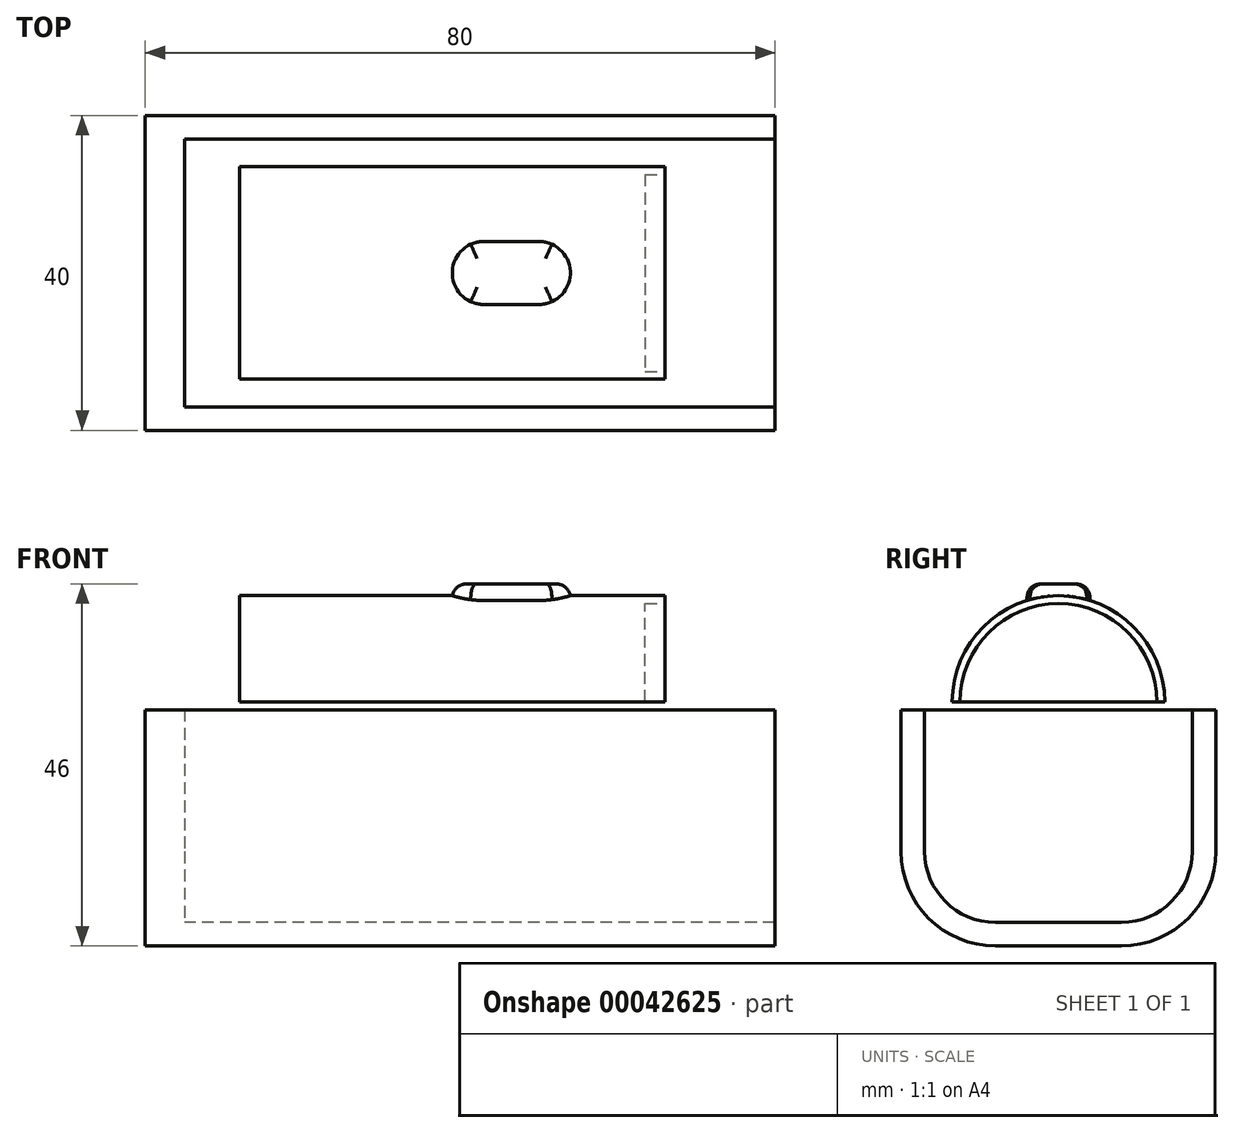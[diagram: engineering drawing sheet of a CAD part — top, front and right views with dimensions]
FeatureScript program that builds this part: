
annotation { "Feature Type Name" : "Feature", "Feature Type Description" : "" }
export const myFeature = defineFeature(function(context is Context, id is Id, definition is map)
    precondition{}
    {
        {
            var Q0;
            Q0=qCreatedBy(makeId("Top.planeOp"),FACE);
            var sketch = newSketch(context, id + "F0", { "sketchPlane" : qUnion([Q0])});
            skCircle(sketch, "E0", {"center": v(0, 0) * mm, "radius": 7 * mm});
            skSolve(sketch);
        }
        {
            var Q0;
            Q0 = qSketchRegion(id + "F0", true);
            extrude(context, id + "F1", {"entities" : qUnion([Q0]), "depth" : 1.5 * mm});
        }
        {
            var Q0;
            Q0=makeQuery(id+"F1.opExtrude","CAP_FACE",FACE,{"disambiguationData":[OSD([sQuery(id+"F0.wireOp",EDGE,"E0")])],"isStart":false});
            var sketch = newSketch(context, id + "F2", { "sketchPlane" : qUnion([Q0])});
            skCircle(sketch, "E1", {"center": v(0, 0) * mm, "radius": 10 * mm});
            skSolve(sketch);
        }
        {
            var Q0;
            Q0 = qSketchRegion(id + "F2", true);
            extrude(context, id + "F3", {"entities" : qUnion([Q0]), "operationType" : NewBodyOperationType.ADD, "depth" : 14 * mm});
        }
        {
            var Q0;
            Q0=qCreatedBy(makeId("Right.planeOp"),FACE);
            var sketch = newSketch(context, id + "F4", { "sketchPlane" : qUnion([Q0])});
            skCircle(sketch, "E2", {"center": v(0, 22) * mm, "radius": 13.5 * mm});
            skSolve(sketch);
        }
        {
            var Q0;
            Q0=makeQuery(id+"F4.imprint","IMPRINT",FACE,{"disambiguationData":[TD([[makeQuery(id+"F4.imprint","IMPRINT",EDGE,{"derivedFrom":sQuery(id+"F4.wireOp",EDGE,"E2")}),1.0]])]});
            extrude(context, id + "F5", {"entities" : qUnion([Q0]), "operationType" : NewBodyOperationType.ADD, "depth" : 36 * mm, "hasSecondDirection" : true, "secondDirectionOppositeDirection" : true, "secondDirectionDepth" : 18 * mm});
        }
        {
            var Q0;
            Q0=makeQuery(id+"F5.opExtrude","CAP_FACE",FACE,{"disambiguationData":[OSD([sQuery(id+"F4.wireOp",EDGE,"E2")])],"isStart":false});
            var sketch = newSketch(context, id + "F6", { "sketchPlane" : qUnion([Q0])});
            skCircle(sketch, "E3.0", {"center": v(0, 22) * mm, "radius": 13.5 * mm});
            skCircle(sketch, "E4", {"center": v(0, 22) * mm, "radius": 12.5 * mm});
            skSolve(sketch);
        }
        {
            var Q0;
            Q0=makeQuery(id+"F6.imprint","IMPRINT",FACE,{"disambiguationData":[TD([[makeQuery(id+"F6.imprint","IMPRINT",EDGE,{"derivedFrom":sQuery(id+"F6.wireOp",EDGE,"E4")}),1.0]])]});
            extrude(context, id + "F7", {"entities" : qUnion([Q0]), "operationType" : NewBodyOperationType.REMOVE, "oppositeDirection" : true, "depth" : 2.5 * mm});
        }
        {
            var Q0;
            Q0=qCreatedBy(makeId("Top.planeOp"),FACE);
            cPlane(context, id + "F8", {"entities" : qUnion([Q0]), "cplaneType" : CPlaneType.OFFSET, "offset" : 33 * mm, "width" : 150 * mm, "height" : 150 * mm});
        }
        {
            var Q0;
            Q0=qCreatedBy(id+"F8.planeOp",FACE);
            var sketch = newSketch(context, id + "F9", { "sketchPlane" : qUnion([Q0])});
            skLineSegment(sketch, "E5.0", {"start": v(36, 13.5) * mm, "end": v(36, -13.5) * mm});
            skLineSegment(sketch, "E6.rect.bottom", {"start": v(20, 4) * mm, "end": v(13, 4) * mm});
            skLineSegment(sketch, "E6.rect.top", {"start": v(20, -4) * mm, "end": v(13, -4) * mm});
            skLineSegment(sketch, "E6.rect.left", {"start": v(24, 0) * mm, "end": v(24, 0) * mm});
            skLineSegment(sketch, "E6.rect.right", {"start": v(9, 0) * mm, "end": v(9, 0) * mm});
            skPoint(sketch, "E6.rect.middle", {"position": v(16.5, 0) * mm});
            skPoint(sketch, "E7.visualSharp", {"position": v(9, -4) * mm});
            skArc(sketch, "E7.filletArc", {"start": v(9, 0) * mm, "mid": v(10.17, -2.83) * mm, "end": v(13, -4) * mm});
            skPoint(sketch, "E8.visualSharp", {"position": v(9, 4) * mm});
            skArc(sketch, "E8.filletArc", {"start": v(13, 4) * mm, "mid": v(10.17, 2.83) * mm, "end": v(9, 0) * mm});
            skPoint(sketch, "E9.visualSharp", {"position": v(24, 4) * mm});
            skArc(sketch, "E9.filletArc", {"start": v(24, 0) * mm, "mid": v(22.83, 2.83) * mm, "end": v(20, 4) * mm});
            skPoint(sketch, "E10.visualSharp", {"position": v(24, -4) * mm});
            skArc(sketch, "E10.filletArc", {"start": v(20, -4) * mm, "mid": v(22.83, -2.83) * mm, "end": v(24, 0) * mm});
            skSolve(sketch);
        }
        {
            var Q0;
            Q0=makeQuery(id+"F9.imprint","IMPRINT",FACE,{"disambiguationData":[TD([[makeQuery(id+"F9.imprint","IMPRINT",EDGE,{"derivedFrom":sQuery(id+"F9.wireOp",EDGE,"E6.rect.bottom")}),1.0]])]});
            extrude(context, id + "F10", {"entities" : qUnion([Q0]), "operationType" : NewBodyOperationType.ADD, "depth" : 4 * mm});
        }
        {
            var Q0;
            Q0=makeQuery(id+"F10.opExtrude","CAP_EDGE",EDGE,{"disambiguationData":[OSD([sQuery(id+"F9.wireOp",EDGE,"E6.rect.top")])],"isStart":false});
            fillet(context, id + "F11", {"entities" : qUnion([Q0]), "radius" : 2 * mm, "tangentPropagation" : true, "rho" : 0.5, "crossSection" : FilletCrossSection.CONIC, "allowEdgeOverflow" : false});
        }
        {
            var Q0;
            Q0=qCreatedBy(makeId("Right.planeOp"),FACE);
            var sketch = newSketch(context, id + "F12", { "sketchPlane" : qUnion([Q0])});
            skLineSegment(sketch, "E11.rect.bottom", {"start": v(-8, -9) * mm, "end": v(8, -9) * mm});
            skLineSegment(sketch, "E11.rect.top", {"start": v(-20, 21) * mm, "end": v(20, 21) * mm});
            skLineSegment(sketch, "E11.rect.left", {"start": v(-20, 3) * mm, "end": v(-20, 21) * mm});
            skLineSegment(sketch, "E11.rect.right", {"start": v(20, 3) * mm, "end": v(20, 21) * mm});
            skPoint(sketch, "E11.rect.middle", {"position": v(0, 6) * mm});
            skPoint(sketch, "E12.visualSharp", {"position": v(20, -9) * mm});
            skArc(sketch, "E12.filletArc", {"start": v(8, -9) * mm, "mid": v(16.49, -5.49) * mm, "end": v(20, 3) * mm});
            skPoint(sketch, "E13.visualSharp", {"position": v(-20, -9) * mm});
            skArc(sketch, "E13.filletArc", {"start": v(-20, 3) * mm, "mid": v(-16.49, -5.49) * mm, "end": v(-8, -9) * mm});
            skSolve(sketch);
        }
        {
            var Q0;
            Q0=makeQuery(id+"F12.imprint","IMPRINT",FACE,{"disambiguationData":[TD([[makeQuery(id+"F12.imprint","IMPRINT",EDGE,{"derivedFrom":sQuery(id+"F12.wireOp",EDGE,"E11.rect.bottom")}),1.0]])]});
            extrude(context, id + "F13", {"entities" : qUnion([Q0]), "depth" : 50 * mm, "hasSecondDirection" : true, "secondDirectionOppositeDirection" : true, "secondDirectionDepth" : 30 * mm});
        }
        {
            var Q0;
            Q0=makeQuery(id+"F13.opExtrude","CAP_FACE",FACE,{"disambiguationData":[OSD([sQuery(id+"F12.wireOp",EDGE,"E11.rect.bottom"),sQuery(id+"F12.wireOp",EDGE,"E11.rect.top"),sQuery(id+"F12.wireOp",EDGE,"E11.rect.left"),sQuery(id+"F12.wireOp",EDGE,"E11.rect.right"),sQuery(id+"F12.wireOp",EDGE,"E12.filletArc"),sQuery(id+"F12.wireOp",EDGE,"E13.filletArc")])],"isStart":true});
            cPlane(context, id + "F14", {"entities" : qUnion([Q0]), "cplaneType" : CPlaneType.OFFSET, "offset" : 5 * mm, "oppositeDirection" : true, "width" : 150 * mm, "height" : 150 * mm});
        }
        {
            var Q0;
            Q0=qCreatedBy(id+"F14.planeOp",FACE);
            var sketch = newSketch(context, id + "F15", { "sketchPlane" : qUnion([Q0])});
            skLineSegment(sketch, "E14.rect.bottom", {"start": v(17, 22) * mm, "end": v(-17, 22) * mm});
            skLineSegment(sketch, "E14.rect.top", {"start": v(8, -6) * mm, "end": v(-8, -6) * mm});
            skLineSegment(sketch, "E14.rect.left", {"start": v(17, 22) * mm, "end": v(17, 3) * mm});
            skLineSegment(sketch, "E14.rect.right", {"start": v(-17, 22) * mm, "end": v(-17, 3) * mm});
            skPoint(sketch, "E14.rect.middle", {"position": v(0, 8) * mm});
            skPoint(sketch, "E15.visualSharp", {"position": v(-17, -6) * mm});
            skArc(sketch, "E15.filletArc", {"start": v(-17, 3) * mm, "mid": v(-14.36, -3.36) * mm, "end": v(-8, -6) * mm});
            skPoint(sketch, "E16.visualSharp", {"position": v(17, -6) * mm});
            skArc(sketch, "E16.filletArc", {"start": v(8, -6) * mm, "mid": v(14.36, -3.36) * mm, "end": v(17, 3) * mm});
            skSolve(sketch);
        }
        {
            var Q0;
            Q0=makeQuery(id+"F15.imprint","IMPRINT",FACE,{"disambiguationData":[TD([[makeQuery(id+"F15.imprint","IMPRINT",EDGE,{"derivedFrom":sQuery(id+"F15.wireOp",EDGE,"E14.rect.bottom")}),1.0]])]});
            extrude(context, id + "F16", {"entities" : qUnion([Q0]), "operationType" : NewBodyOperationType.REMOVE, "oppositeDirection" : true, "depth" : 80 * mm});
        }
    });
